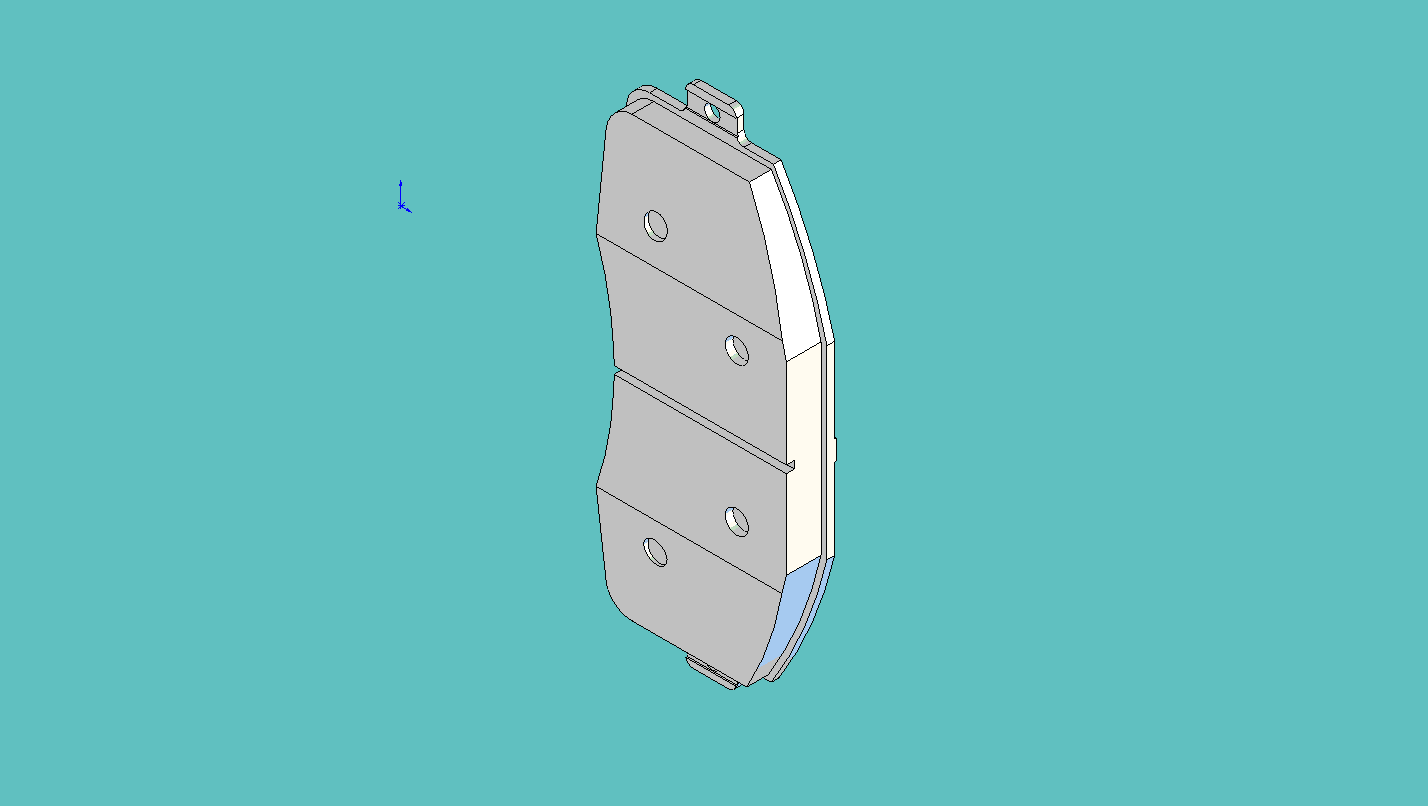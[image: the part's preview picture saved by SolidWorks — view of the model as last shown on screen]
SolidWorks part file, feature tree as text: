
SOLIDWORKS PART (.sldprt)
format: sldprt  version: not decoded by parser v0  size: 321,024 bytes
history: native  units: mm
features: sketch x13, cut_extrude x8, extrude x5, material x1, fillet x1 (+13 scaffold rows collapsed)
feature tree (41):
  scaffold x13  (default folders/planes/origin — collapsed)
  material  "Material <not specified>"
  sketch  "Sketch2"
  extrude  "Extrude1"  Depth=11.43mm
  sketch  "Sketch3"
  cut_extrude  "Cut-Extrude2"  [1 undecoded]
  fillet  "Fillet1"  Radius=7.62mm
  sketch  "Sketch4"
  cut_extrude  "Cut-Extrude3"  [1 undecoded]
  sketch  "Sketch5"  dims[D1=279.4mm]
  cut_extrude  "Cut-Extrude4"  Depth=25.908mm
  sketch  "Sketch6"
  cut_extrude  "Cut-Extrude5"  [1 undecoded]
  sketch  "Sketch7"  dims[D1=~15.437436mm]
  cut_extrude  "Cut-Extrude6"  Depth=2.54mm
  sketch  "Sketch11"  dims[c1.D1=2.54mm c1.D2=2.54mm c2.D1=2.54mm]
  extrude  "Extrude2"  Depth=2.54mm
  sketch  "Sketch13"  dims[D1=50.0mm]
  extrude  "Extrude4"  Depth=0.635mm
  sketch  "Sketch14"  dims[D1=43.18mm]
  cut_extrude  "Cut-Extrude7"  Depth=2.54mm
  sketch  "Sketch15"  dims[c1.D1=15.24mm c1.D2=10.16mm c1.D3=10.16mm c2.D1=~27.931795mm c2.D2=~19.65412mm]
  extrude  "Extrude5"  Depth=2.54mm
  sketch  "Sketch16"  dims[D1=5.08mm]
  cut_extrude  "Cut-Extrude8"  [1 undecoded]
  sketch  "Sketch17"
  cut_extrude  "Cut-Extrude9"  Depth=0.508mm
  sketch  "Sketch18"
  extrude  "Extrude6"  Depth=0.508mm
decode coverage: 17 of 27 modeling features carry decoded parameters
note: ~ marks probable driven/reference dimensions
note: 4 parameter values undecoded
summary: no parameter record found for 4 features
note: suppression state not decoded; provenance and decode notes live in map.json
